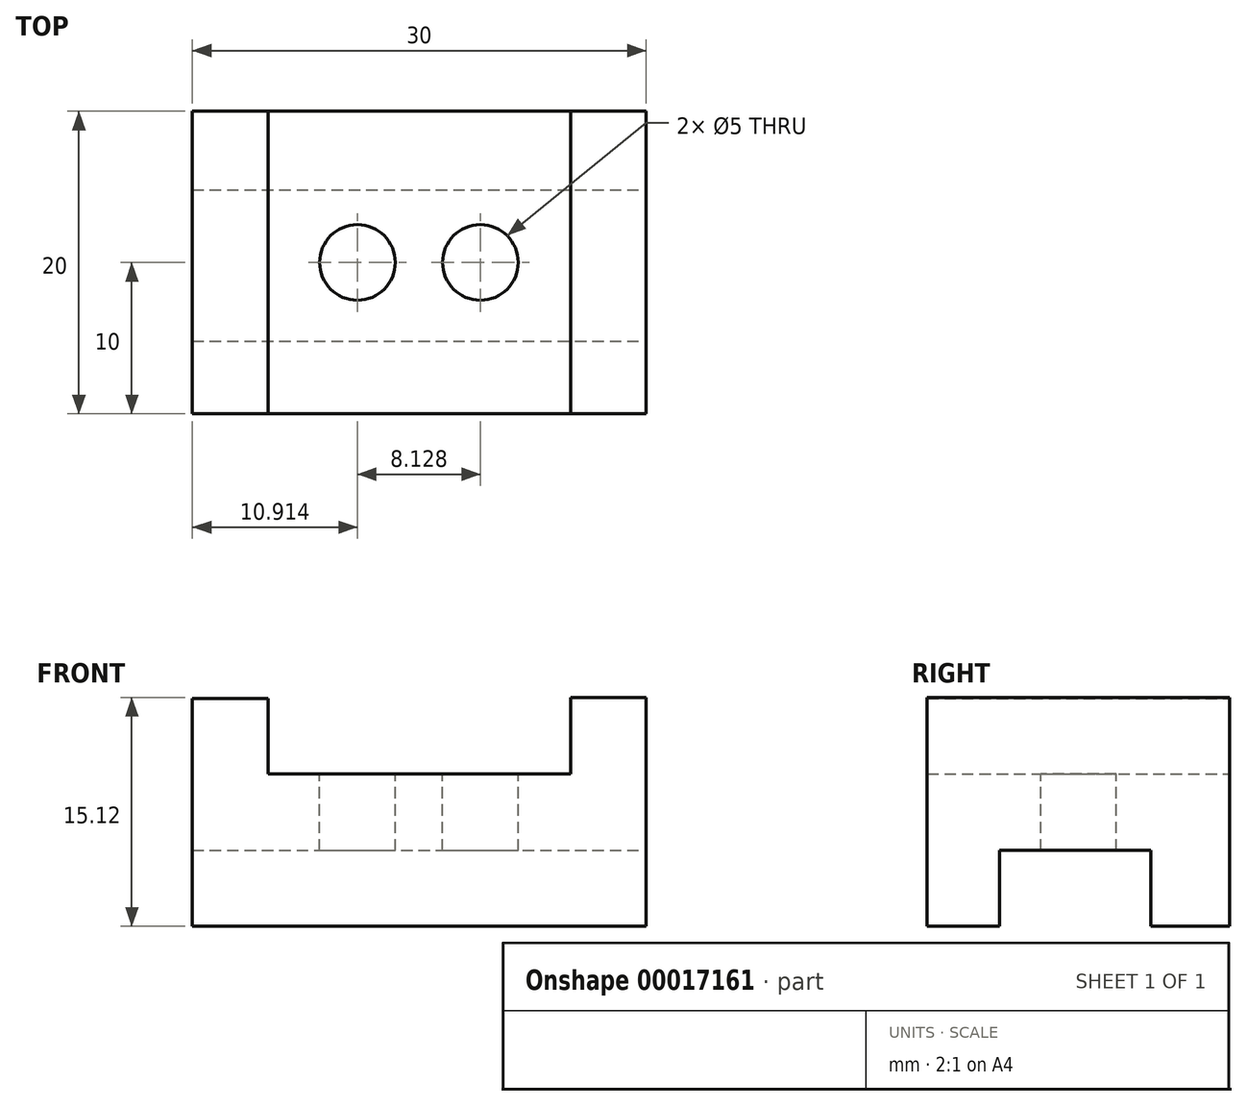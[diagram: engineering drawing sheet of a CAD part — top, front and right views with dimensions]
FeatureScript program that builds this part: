
annotation { "Feature Type Name" : "Feature", "Feature Type Description" : "" }
export const myFeature = defineFeature(function(context is Context, id is Id, definition is map)
    precondition{}
    {
        {
            var Q0;
            Q0=qCreatedBy(makeId("Front.planeOp"),FACE);
            var sketch = newSketch(context, id + "F0", { "sketchPlane" : qUnion([Q0])});
            skLineSegment(sketch, "E0", {"start": v(-28.02, 0) * mm, "end": v(-28.02, 5) * mm});
            skLineSegment(sketch, "E1", {"start": v(-28.02, 5) * mm, "end": v(-23.02, 5) * mm});
            skLineSegment(sketch, "E2", {"start": v(-23.02, 5) * mm, "end": v(-23.02, 0) * mm});
            skLineSegment(sketch, "E3", {"start": v(-23.02, 0) * mm, "end": v(-3.02, 0) * mm});
            skLineSegment(sketch, "E4", {"start": v(-3.02, 0) * mm, "end": v(-3.02, 5.06) * mm});
            skLineSegment(sketch, "E5", {"start": v(-3.02, 5.06) * mm, "end": v(1.98, 5.06) * mm});
            skLineSegment(sketch, "E6", {"start": v(1.98, 5.06) * mm, "end": v(1.98, 0) * mm});
            skLineSegment(sketch, "E7", {"start": v(1.98, 0) * mm, "end": v(1.98, -10.06) * mm});
            skLineSegment(sketch, "E8", {"start": v(1.98, -10.06) * mm, "end": v(-28.02, -10.06) * mm});
            skLineSegment(sketch, "E9", {"start": v(-28.02, 0) * mm, "end": v(-28.02, -10.06) * mm});
            skSolve(sketch);
        }
        {
            var Q0;
            Q0 = qSketchRegion(id + "F0", true);
            extrude(context, id + "F1", {"entities" : qUnion([Q0]), "depth" : 20 * mm});
        }
        {
            var Q0;
            Q0=makeQuery(id+"F1.opExtrude","SWEPT_FACE",FACE,{"disambiguationData":[OSD([sQuery(id+"F0.wireOp",EDGE,"E6"),sQuery(id+"F0.wireOp",EDGE,"E7")])]});
            var sketch = newSketch(context, id + "F2", { "sketchPlane" : qUnion([Q0])});
            skLineSegment(sketch, "E10.bottom", {"start": v(-15.2, -10.06) * mm, "end": v(-5.2, -10.06) * mm});
            skLineSegment(sketch, "E10.top", {"start": v(-15.2, -5.06) * mm, "end": v(-5.2, -5.06) * mm});
            skLineSegment(sketch, "E10.left", {"start": v(-15.2, -10.06) * mm, "end": v(-15.2, -5.06) * mm});
            skLineSegment(sketch, "E10.right", {"start": v(-5.2, -10.06) * mm, "end": v(-5.2, -5.06) * mm});
            skLineSegment(sketch, "E11.left", {"start": v(-15.2, -10.06) * mm, "end": v(-15.2, -10.06) * mm});
            skLineSegment(sketch, "E11.right", {"start": v(-5.2, -10.06) * mm, "end": v(-5.2, -10.06) * mm});
            skSolve(sketch);
        }
        {
            var Q0;
            Q0 = qSketchRegion(id + "F2", true);
            extrude(context, id + "F3", {"entities" : qUnion([Q0]), "operationType" : NewBodyOperationType.REMOVE, "endBound" : BoundingType.THROUGH_ALL, "oppositeDirection" : true, "depth" : 25 * mm});
        }
        {
            var Q0;
            Q0=makeQuery(id+"F1.opExtrude","SWEPT_FACE",FACE,{"disambiguationData":[OSD([sQuery(id+"F0.wireOp",EDGE,"E3")])]});
            var sketch = newSketch(context, id + "F4", { "sketchPlane" : qUnion([Q0])});
            skCircle(sketch, "E12", {"center": v(-17.1, -10) * mm, "radius": 2.5 * mm});
            skCircle(sketch, "E13", {"center": v(-8.98, -10) * mm, "radius": 2.5 * mm});
            skSolve(sketch);
        }
        {
            var Q0;
            Q0 = qSketchRegion(id + "F4", true);
            extrude(context, id + "F5", {"entities" : qUnion([Q0]), "operationType" : NewBodyOperationType.REMOVE, "endBound" : BoundingType.THROUGH_ALL, "oppositeDirection" : true, "depth" : 25 * mm});
        }
    });
